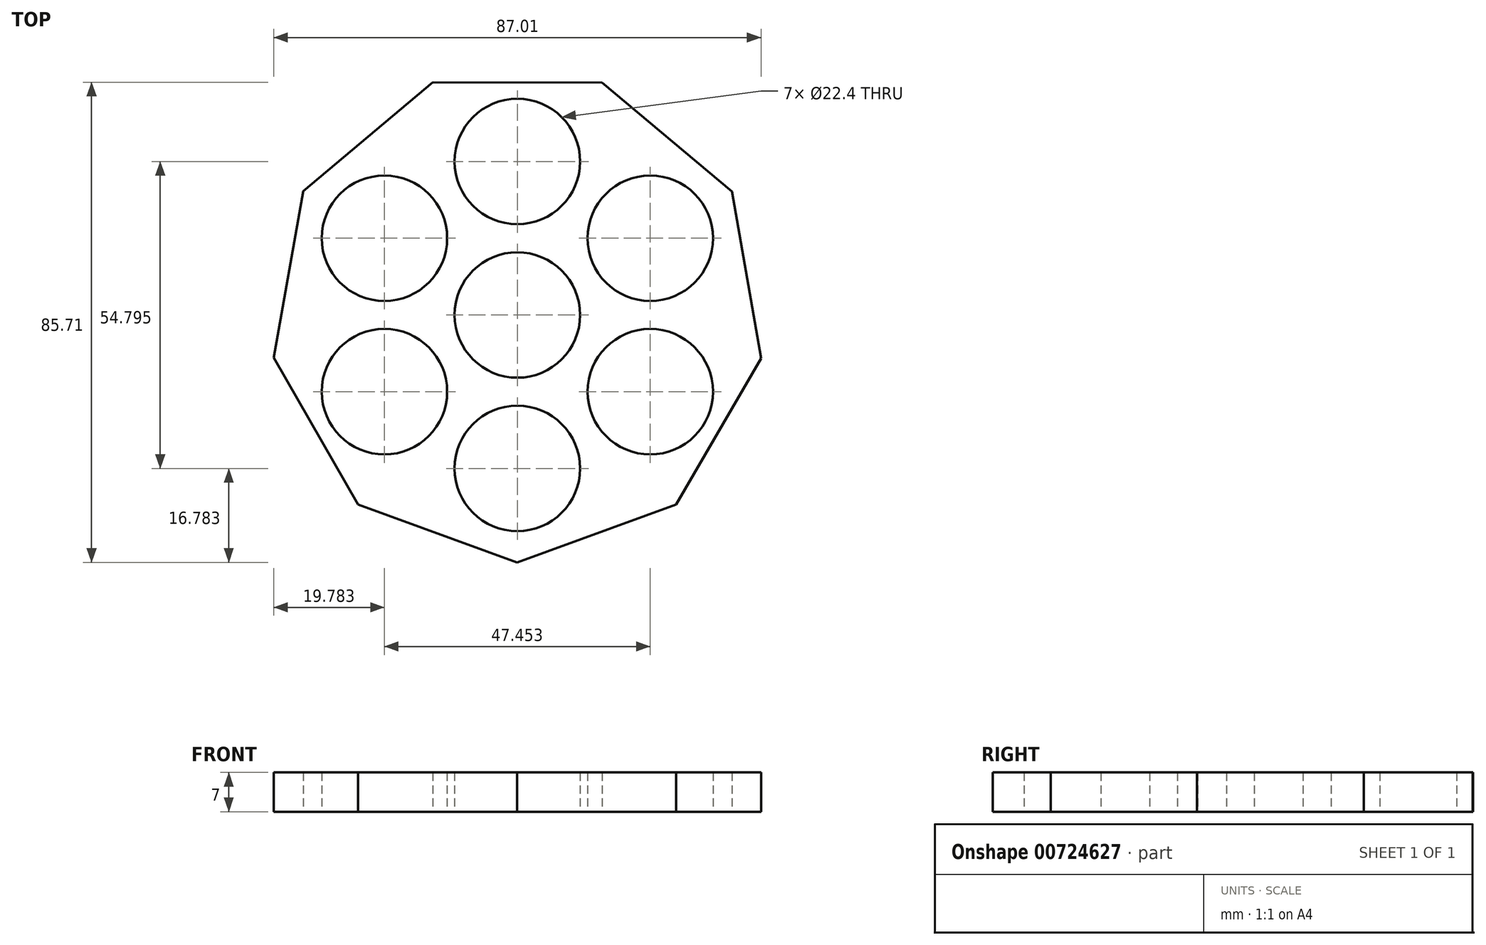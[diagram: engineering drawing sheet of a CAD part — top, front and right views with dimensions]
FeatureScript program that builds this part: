
annotation { "Feature Type Name" : "Feature", "Feature Type Description" : "" }
export const myFeature = defineFeature(function(context is Context, id is Id, definition is map)
    precondition{}
    {
        {
            var Q0;
            Q0=qCreatedBy(makeId("Top.planeOp"),FACE);
            var sketch = newSketch(context, id + "F0", { "sketchPlane" : qUnion([Q0])});
            skCircle(sketch, "E0", {"center": v(0, 0) * mm, "radius": 11.2 * mm});
            skCircle(sketch, "E1", {"center": v(0, 0) * mm, "radius": 13.2 * mm});
            skCircle(sketch, "E2.cCircle", {"center": v(0, 0) * mm, "radius": 41.51 * mm, "construction": true});
            skLineSegment(sketch, "E2.0", {"start": v(43.5, -7.71) * mm, "end": v(28.37, -33.87) * mm});
            skLineSegment(sketch, "E2.1", {"start": v(28.37, -33.87) * mm, "end": v(-0.04, -44.18) * mm});
            skLineSegment(sketch, "E2.2", {"start": v(-0.04, -44.18) * mm, "end": v(-28.43, -33.82) * mm});
            skLineSegment(sketch, "E2.3", {"start": v(-28.43, -33.82) * mm, "end": v(-43.51, -7.63) * mm});
            skLineSegment(sketch, "E2.4", {"start": v(-43.51, -7.63) * mm, "end": v(-38.24, 22.12) * mm});
            skLineSegment(sketch, "E2.5", {"start": v(-38.24, 22.12) * mm, "end": v(-15.07, 41.53) * mm});
            skLineSegment(sketch, "E2.6", {"start": v(-15.07, 41.53) * mm, "end": v(15.15, 41.5) * mm});
            skLineSegment(sketch, "E2.7", {"start": v(15.15, 41.5) * mm, "end": v(38.28, 22.05) * mm});
            skLineSegment(sketch, "E2.8", {"start": v(38.28, 22.05) * mm, "end": v(43.5, -7.71) * mm});
            skPoint(sketch, "E2.0.midPoint", {"position": v(35.93, -20.79) * mm});
            skCircle(sketch, "E3", {"center": v(0, 27.4) * mm, "radius": 13.2 * mm});
            skCircle(sketch, "E4", {"center": v(0, 27.4) * mm, "radius": 11.2 * mm});
            skCircle(sketch, "E5.1.0", {"center": v(-23.73, 13.7) * mm, "radius": 11.2 * mm});
            skCircle(sketch, "E5.1.1", {"center": v(-23.73, 13.7) * mm, "radius": 13.2 * mm});
            skCircle(sketch, "E5.2.0", {"center": v(-23.73, -13.7) * mm, "radius": 11.2 * mm});
            skCircle(sketch, "E5.2.1", {"center": v(-23.73, -13.7) * mm, "radius": 13.2 * mm});
            skCircle(sketch, "E5.3.0", {"center": v(0, -27.4) * mm, "radius": 11.2 * mm});
            skCircle(sketch, "E5.3.1", {"center": v(0, -27.4) * mm, "radius": 13.2 * mm});
            skCircle(sketch, "E5.4.0", {"center": v(23.73, -13.7) * mm, "radius": 11.2 * mm});
            skCircle(sketch, "E5.4.1", {"center": v(23.73, -13.7) * mm, "radius": 13.2 * mm});
            skCircle(sketch, "E5.5.0", {"center": v(23.73, 13.7) * mm, "radius": 11.2 * mm});
            skCircle(sketch, "E5.5.1", {"center": v(23.73, 13.7) * mm, "radius": 13.2 * mm});
            skSolve(sketch);
        }
        {
            var Q0;
            Q0=makeQuery(id+"F0.imprint","IMPRINT",FACE,{"disambiguationData":[TD([[makeQuery(id+"F0.imprint","IMPRINT",EDGE,{"derivedFrom":sQuery(id+"F0.wireOp",EDGE,"E1")}),-1.0]])]});
            var Q1;
            Q1=makeQuery(id+"F0.imprint","IMPRINT",FACE,{"disambiguationData":[TD([[makeQuery(id+"F0.imprint","IMPRINT",EDGE,{"derivedFrom":sQuery(id+"F0.wireOp",EDGE,"E5.1.0")}),-1.0]])]});
            var Q2;
            Q2=makeQuery(id+"F0.imprint","IMPRINT",FACE,{"disambiguationData":[TD([[makeQuery(id+"F0.imprint","IMPRINT",EDGE,{"derivedFrom":sQuery(id+"F0.wireOp",EDGE,"E3")}),1.0]])]});
            var Q3;
            Q3=makeQuery(id+"F0.imprint","IMPRINT",FACE,{"disambiguationData":[TD([[makeQuery(id+"F0.imprint","IMPRINT",EDGE,{"derivedFrom":sQuery(id+"F0.wireOp",EDGE,"E5.5.0")}),-1.0]])]});
            var Q4;
            Q4=makeQuery(id+"F0.imprint","IMPRINT",FACE,{"disambiguationData":[TD([[makeQuery(id+"F0.imprint","IMPRINT",EDGE,{"derivedFrom":sQuery(id+"F0.wireOp",EDGE,"E5.4.0")}),-1.0]])]});
            var Q5;
            Q5=makeQuery(id+"F0.imprint","IMPRINT",FACE,{"disambiguationData":[TD([[makeQuery(id+"F0.imprint","IMPRINT",EDGE,{"derivedFrom":sQuery(id+"F0.wireOp",EDGE,"E5.3.0")}),-1.0]])]});
            var Q6;
            Q6=makeQuery(id+"F0.imprint","IMPRINT",FACE,{"disambiguationData":[TD([[makeQuery(id+"F0.imprint","IMPRINT",EDGE,{"derivedFrom":sQuery(id+"F0.wireOp",EDGE,"E5.2.0")}),-1.0]])]});
            var Q7;
            Q7=makeQuery(id+"F0.imprint","IMPRINT",FACE,{"disambiguationData":[TD([[makeQuery(id+"F0.imprint","IMPRINT",EDGE,{"derivedFrom":sQuery(id+"F0.wireOp",EDGE,"E0")}),-1.0]])]});
            extrude(context, id + "F1", {"entities" : qUnion([Q0, Q1, Q2, Q3, Q4, Q5, Q6, Q7]), "depth" : 7 * mm, "offsetDistance" : 25 * mm});
        }
    });
